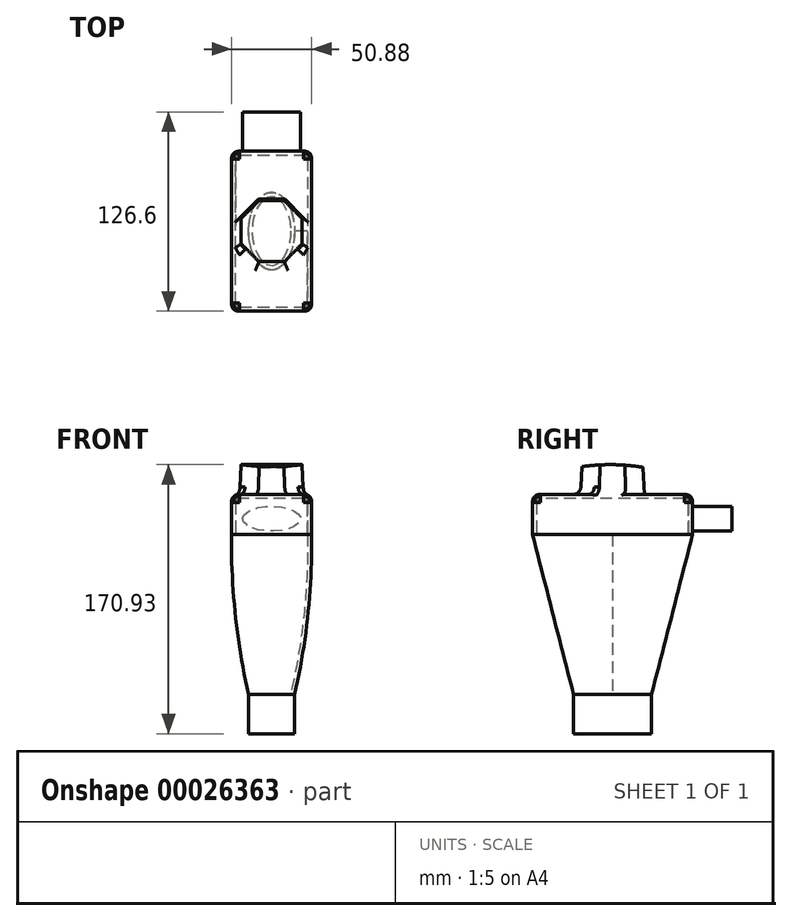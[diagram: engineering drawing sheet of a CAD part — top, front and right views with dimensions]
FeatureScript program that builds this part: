
annotation { "Feature Type Name" : "Feature", "Feature Type Description" : "" }
export const myFeature = defineFeature(function(context is Context, id is Id, definition is map)
    precondition{}
    {
        {
            var Q0;
            Q0=qCreatedBy(makeId("Top.planeOp"),FACE);
            var sketch = newSketch(context, id + "F0", { "sketchPlane" : qUnion([Q0])});
            skLineSegment(sketch, "E0.rect.bottom", {"start": v(-25.4, 50.8) * mm, "end": v(25.4, 50.8) * mm});
            skLineSegment(sketch, "E0.rect.top", {"start": v(-25.4, -50.8) * mm, "end": v(25.4, -50.8) * mm});
            skLineSegment(sketch, "E0.rect.left", {"start": v(-25.4, 50.8) * mm, "end": v(-25.4, -50.8) * mm});
            skLineSegment(sketch, "E0.rect.right", {"start": v(25.4, 50.8) * mm, "end": v(25.4, -50.8) * mm});
            skPoint(sketch, "E0.rect.middle", {"position": v(0, 0) * mm});
            skSolve(sketch);
        }
        {
            var Q0;
            Q0 = qSketchRegion(id + "F0", true);
            extrude(context, id + "F1", {"entities" : qUnion([Q0]), "depth" : 25.4 * mm});
        }
        {
            var Q0;
            Q0=makeQuery(id+"F1.opExtrude","CAP_EDGE",EDGE,{"disambiguationData":[OSD([sQuery(id+"F0.wireOp",EDGE,"E0.rect.top")])],"isStart":false});
            var Q1;
            Q1=makeQuery(id+"F1.opExtrude","CAP_EDGE",EDGE,{"disambiguationData":[OSD([sQuery(id+"F0.wireOp",EDGE,"E0.rect.right")])],"isStart":false});
            var Q2;
            Q2=makeQuery(id+"F1.opExtrude","CAP_EDGE",EDGE,{"disambiguationData":[OSD([sQuery(id+"F0.wireOp",EDGE,"E0.rect.bottom")])],"isStart":false});
            var Q3;
            Q3=makeQuery(id+"F1.opExtrude","CAP_EDGE",EDGE,{"disambiguationData":[OSD([sQuery(id+"F0.wireOp",EDGE,"E0.rect.left")])],"isStart":false});
            var Q4;
            Q4=makeQuery(id+"F1.opExtrude","SWEPT_EDGE",EDGE,{"disambiguationData":[OSD([sQuery(id+"F0.wireOp",EDGE,"E0.rect.top"),sQuery(id+"F0.wireOp",EDGE,"E0.rect.right")])]});
            var Q5;
            Q5=makeQuery(id+"F1.opExtrude","SWEPT_EDGE",EDGE,{"disambiguationData":[OSD([sQuery(id+"F0.wireOp",EDGE,"E0.rect.top"),sQuery(id+"F0.wireOp",EDGE,"E0.rect.left")])]});
            var Q6;
            Q6=makeQuery(id+"F1.opExtrude","SWEPT_EDGE",EDGE,{"disambiguationData":[OSD([sQuery(id+"F0.wireOp",EDGE,"E0.rect.bottom"),sQuery(id+"F0.wireOp",EDGE,"E0.rect.right")])]});
            var Q7;
            Q7=makeQuery(id+"F1.opExtrude","SWEPT_EDGE",EDGE,{"disambiguationData":[OSD([sQuery(id+"F0.wireOp",EDGE,"E0.rect.bottom"),sQuery(id+"F0.wireOp",EDGE,"E0.rect.left")])]});
            fillet(context, id + "F2", {"entities" : qUnion([Q0, Q1, Q2, Q3, Q4, Q5, Q6, Q7]), "radius" : 5.08 * mm, "tangentPropagation" : true, "rho" : 0.5, "crossSection" : FilletCrossSection.CONIC, "allowEdgeOverflow" : false});
        }
        {
            var Q0;
            Q0=makeQuery(id+"F1.opExtrude","CAP_FACE",FACE,{"disambiguationData":[OSD([sQuery(id+"F0.wireOp",EDGE,"E0.rect.bottom"),sQuery(id+"F0.wireOp",EDGE,"E0.rect.top"),sQuery(id+"F0.wireOp",EDGE,"E0.rect.left"),sQuery(id+"F0.wireOp",EDGE,"E0.rect.right")])],"isStart":true});
            cPlane(context, id + "F3", {"entities" : qUnion([Q0]), "cplaneType" : CPlaneType.OFFSET, "offset" : 101.6 * mm, "width" : 152.4 * mm, "height" : 152.4 * mm});
        }
        {
            var Q0;
            Q0=qCreatedBy(id+"F3.planeOp",FACE);
            var sketch = newSketch(context, id + "F4", { "sketchPlane" : qUnion([Q0])});
            skEllipse(sketch, "E1", {"center": v(0, 0) * mm, "majorRadius": 24.72 * mm, "minorRadius": 14.6 * mm, "majorAxis": v(0, 1)});
            skSolve(sketch);
        }
        {
            var Q0;
            Q0=qCreatedBy(makeId("Front.planeOp"),FACE);
            var sketch = newSketch(context, id + "F5", { "sketchPlane" : qUnion([Q0])});
            skArc(sketch, "E2", {"start": v(14.6, -101.6) * mm, "mid": v(23.05, -51.12) * mm, "end": v(25.4, 0) * mm});
            skLineSegment(sketch, "E3", {"start": v(0, 0) * mm, "end": v(0, -101.81) * mm, "construction": true});
            skArc(sketch, "E4.MirrorCS", {"start": v(-14.6, -101.6) * mm, "mid": v(-23.05, -51.12) * mm, "end": v(-25.4, 0) * mm});
            skSolve(sketch);
        }
        {
            var Q1;
            Q1=makeQuery(id+"F1.opExtrude","CAP_FACE",FACE,{"disambiguationData":[OSD([sQuery(id+"F0.wireOp",EDGE,"E0.rect.bottom"),sQuery(id+"F0.wireOp",EDGE,"E0.rect.top"),sQuery(id+"F0.wireOp",EDGE,"E0.rect.left"),sQuery(id+"F0.wireOp",EDGE,"E0.rect.right")])],"isStart":true});
            var Q2;
            Q2=makeQuery(id+"F4.imprint","IMPRINT",FACE,{"disambiguationData":[TD([[makeQuery(id+"F4.imprint","IMPRINT",EDGE,{"derivedFrom":sQuery(id+"F4.wireOp",EDGE,"E1")}),1.0]])]});
            var Q3;
            Q3=sQuery(id+"F5.wireOp",EDGE,"E2");
            var Q4;
            Q4=sQuery(id+"F5.wireOp",EDGE,"E4.MirrorCS");
            loft(context, id + "F6", {"operationType" : NewBodyOperationType.ADD, "addGuides" : true, "sheetProfilesArray" : [{ "sheetProfileEntities" : qUnion([Q1]) }, { "sheetProfileEntities" : qUnion([Q2]) }], "guidesArray" : [{ "guideEntities" : qUnion([Q3]), "guideDerivativeType" : LoftGuideDerivativeType.DEFAULT, "guideDerivativeMagnitude" : 1 }, { "guideEntities" : qUnion([Q4]), "guideDerivativeType" : LoftGuideDerivativeType.DEFAULT, "guideDerivativeMagnitude" : 1 }]});
        }
        {
            var Q0;
            Q0=makeQuery(id+"F6.opLoft","CAP_FACE",FACE,{"disambiguationData":[OSD([makeQuery(id+"F4.imprint","IMPRINT",FACE,{"disambiguationData":[TD([[makeQuery(id+"F4.imprint","IMPRINT",EDGE,{"derivedFrom":sQuery(id+"F4.wireOp",EDGE,"E1")}),1.0]])]})])],"isStart":true});
            shell(context, id + "F7", {"entities" : qUnion([Q0]), "thickness" : 2.5 * mm});
        }
        {
            var Q0;
            Q0=qCreatedBy(makeId("Right.planeOp"),FACE);
            var sketch = newSketch(context, id + "F8", { "sketchPlane" : qUnion([Q0])});
            skArc(sketch, "E5", {"start": v(71.34, 21.87) * mm, "mid": v(-1.54, 44.33) * mm, "end": v(-74.42, 21.87) * mm});
            skSolve(sketch);
        }
        {
            var Q0;
            Q0=sQuery(id+"F8.wireOp",EDGE,"E5");
            extrude(context, id + "F9", {"bodyType" : ToolBodyType.SURFACE, "surfaceEntities" : qUnion([Q0]), "depth" : 25 * mm, "hasSecondDirection" : true, "secondDirectionOppositeDirection" : true, "secondDirectionDepth" : 25 * mm});
        }
        {
            var Q0;
            Q0=makeQuery(id+"F4.imprint","IMPRINT",FACE,{"disambiguationData":[TD([[makeQuery(id+"F4.imprint","IMPRINT",EDGE,{"derivedFrom":sQuery(id+"F4.wireOp",EDGE,"E1")}),1.0]])]});
            var sketch = newSketch(context, id + "F10", { "sketchPlane" : qUnion([Q0])});
            skEllipse(sketch, "E6.0", {"center": v(0, 0) * mm, "majorRadius": 24.72 * mm, "minorRadius": 14.6 * mm, "majorAxis": v(0, 1)});
            skFitSpline(sketch, "E7.0", {"points": [v(6.07, 18.9) * mm, v(5.05, 19.91) * mm, v(4.15, 20.63) * mm, v(3.44, 21.1) * mm, v(2.68, 21.51) * mm, v(1.88, 21.84) * mm, v(1.05, 22.06) * mm, v(0.18, 22.16) * mm, v(-0.68, 22.12) * mm, v(-1.38, 21.97) * mm, v(-1.94, 21.8) * mm, v(-2.47, 21.6) * mm, v(-3.1, 21.3) * mm, v(-3.83, 20.85) * mm, v(-4.52, 20.34) * mm, v(-5.17, 19.78) * mm, v(-5.98, 18.99) * mm, v(-6.9, 17.9) * mm, v(-7.86, 16.49) * mm, v(-8.7, 15) * mm, v(-9.44, 13.45) * mm, v(-10.28, 11.33) * mm, v(-11.09, 8.62) * mm, v(-11.62, 5.8) * mm, v(-11.88, 3.54) * mm, v(-12, 1.84) * mm, v(-12.04, 0.14) * mm, v(-12.02, -1.56) * mm, v(-11.9, -3.27) * mm, v(-11.72, -4.96) * mm, v(-11.46, -6.63) * mm, v(-11.12, -8.29) * mm, v(-10.7, -9.92) * mm, v(-10.19, -11.53) * mm, v(-9.58, -13.12) * mm, v(-8.86, -14.68) * mm, v(-8.05, -16.18) * mm, v(-7.1, -17.61) * mm, v(-6.2, -18.73) * mm, v(-5.41, -19.56) * mm, v(-4.77, -20.14) * mm, v(-4.1, -20.66) * mm, v(-3.38, -21.13) * mm, v(-2.62, -21.54) * mm, v(-1.82, -21.86) * mm, v(-1, -22.07) * mm, v(-0.12, -22.16) * mm, v(0.74, -22.1) * mm, v(1.44, -21.96) * mm, v(1.99, -21.78) * mm, v(2.52, -21.58) * mm, v(3.15, -21.26) * mm, v(3.87, -20.82) * mm, v(4.56, -20.31) * mm, v(5.2, -19.75) * mm, v(6.01, -18.95) * mm, v(6.92, -17.87) * mm, v(7.88, -16.45) * mm, v(8.72, -14.97) * mm, v(9.45, -13.42) * mm, v(10.29, -11.3) * mm, v(11.1, -8.6) * mm, v(11.62, -5.79) * mm, v(11.88, -3.53) * mm, v(12, -1.84) * mm, v(12.04, -0.15) * mm, v(12.02, 1.54) * mm, v(11.9, 3.22) * mm, v(11.73, 4.9) * mm, v(11.47, 6.58) * mm, v(11.01, 8.82) * mm, v(10.4, 10.99) * mm, v(9.6, 13.09) * mm, v(8.9, 14.62) * mm, v(8.09, 16.12) * mm, v(7.15, 17.56) * mm, v(6.07, 18.9) * mm, v(5.05, 19.91) * mm, v(4.15, 20.63) * mm, v(6.07, 18.9) * mm]});
            skSolve(sketch);
        }
        {
            var Q0;
            Q0 = qSketchRegion(id + "F10", true);
            extrude(context, id + "F11", {"entities" : qUnion([Q0]), "operationType" : NewBodyOperationType.ADD, "depth" : 25 * mm});
        }
        {
            var Q0;
            Q0=makeQuery(id+"F1.opExtrude","CAP_FACE",FACE,{"disambiguationData":[OSD([sQuery(id+"F0.wireOp",EDGE,"E0.rect.bottom"),sQuery(id+"F0.wireOp",EDGE,"E0.rect.top"),sQuery(id+"F0.wireOp",EDGE,"E0.rect.left"),sQuery(id+"F0.wireOp",EDGE,"E0.rect.right")])],"isStart":false});
            var sketch = newSketch(context, id + "F12", { "sketchPlane" : qUnion([Q0])});
            skCircle(sketch, "E8.cCircle", {"center": v(0, 0) * mm, "radius": 20.32 * mm, "construction": true});
            skLineSegment(sketch, "E8.0", {"start": v(20.32, 8.42) * mm, "end": v(20.32, -8.42) * mm});
            skLineSegment(sketch, "E8.1", {"start": v(20.32, -8.42) * mm, "end": v(8.42, -20.32) * mm});
            skLineSegment(sketch, "E8.2", {"start": v(8.42, -20.32) * mm, "end": v(-8.42, -20.32) * mm});
            skLineSegment(sketch, "E8.3", {"start": v(-8.42, -20.32) * mm, "end": v(-20.32, -8.42) * mm});
            skLineSegment(sketch, "E8.4", {"start": v(-20.32, -8.42) * mm, "end": v(-20.32, 8.42) * mm});
            skLineSegment(sketch, "E8.5", {"start": v(-20.32, 8.42) * mm, "end": v(-8.42, 20.32) * mm});
            skLineSegment(sketch, "E8.6", {"start": v(-8.42, 20.32) * mm, "end": v(8.42, 20.32) * mm});
            skLineSegment(sketch, "E8.7", {"start": v(8.42, 20.32) * mm, "end": v(20.32, 8.42) * mm});
            skPoint(sketch, "E8.0.midPoint", {"position": v(20.32, 0) * mm});
            skSolve(sketch);
        }
        {
            var Q0;
            Q0 = qSketchRegion(id + "F12", true);
            var Q1;
            Q1=makeQuery(id+"F9.opExtrude","SWEPT_FACE",FACE,{"disambiguationData":[OSD([sQuery(id+"F8.wireOp",EDGE,"E5")])]});
            extrude(context, id + "F13", {"entities" : qUnion([Q0]), "operationType" : NewBodyOperationType.ADD, "endBound" : BoundingType.UP_TO_SURFACE, "endBoundEntityFace" : qUnion([Q1]), "depth" : 25 * mm, "hasDraft" : true, "draftAngle" : 3 * degree, "draftPullDirection" : true});
        }
        {
            var Q0;
            Q0=makeQuery(id+"F13.opExtrude","CAP_EDGE",EDGE,{"disambiguationData":[OSD([sQuery(id+"F12.wireOp",EDGE,"E8.6")])],"isStart":true});
            var Q1;
            Q1=makeQuery(id+"F13.opExtrude","CAP_EDGE",EDGE,{"disambiguationData":[OSD([sQuery(id+"F12.wireOp",EDGE,"E8.5")])],"isStart":true});
            var Q2;
            {var subQ0=sQuery(id+"F0.wireOp",EDGE,"E0.rect.left");Q2=makeQuery(id+"F13.boolean.opBoolean","MERGE",EDGE,{"derivedFrom":[makeQuery(id+"F2.opFillet","BLEND_EDGE",EDGE,{"blendedFrom":[makeQuery(id+"F1.opExtrude","CAP_EDGE",EDGE,{"disambiguationData":[OSD([subQ0])],"isStart":false}),makeQuery(id+"F1.opExtrude","CAP_FACE",FACE,{"disambiguationData":[OSD([sQuery(id+"F0.wireOp",EDGE,"E0.rect.bottom"),sQuery(id+"F0.wireOp",EDGE,"E0.rect.top"),subQ0,sQuery(id+"F0.wireOp",EDGE,"E0.rect.right")])],"isStart":false})],"blendedInto":[makeQuery(id+"F1.opExtrude","CAP_FACE",FACE,{"disambiguationData":[OSD([sQuery(id+"F0.wireOp",EDGE,"E0.rect.bottom"),sQuery(id+"F0.wireOp",EDGE,"E0.rect.top"),subQ0,sQuery(id+"F0.wireOp",EDGE,"E0.rect.right")])],"isStart":false})]}),makeQuery(id+"F13.opExtrude","CAP_EDGE",EDGE,{"disambiguationData":[OSD([sQuery(id+"F12.wireOp",EDGE,"E8.4")])],"isStart":true})]});}
            var Q3;
            Q3=makeQuery(id+"F13.opExtrude","CAP_EDGE",EDGE,{"disambiguationData":[OSD([sQuery(id+"F12.wireOp",EDGE,"E8.3")])],"isStart":true});
            var Q4;
            Q4=makeQuery(id+"F13.opExtrude","CAP_EDGE",EDGE,{"disambiguationData":[OSD([sQuery(id+"F12.wireOp",EDGE,"E8.2")])],"isStart":true});
            var Q5;
            Q5=makeQuery(id+"F13.opExtrude","CAP_EDGE",EDGE,{"disambiguationData":[OSD([sQuery(id+"F12.wireOp",EDGE,"E8.1")])],"isStart":true});
            var Q6;
            {var subQ0=sQuery(id+"F0.wireOp",EDGE,"E0.rect.right");Q6=makeQuery(id+"F13.boolean.opBoolean","MERGE",EDGE,{"derivedFrom":[makeQuery(id+"F2.opFillet","BLEND_EDGE",EDGE,{"blendedFrom":[makeQuery(id+"F1.opExtrude","CAP_EDGE",EDGE,{"disambiguationData":[OSD([subQ0])],"isStart":false}),makeQuery(id+"F1.opExtrude","CAP_FACE",FACE,{"disambiguationData":[OSD([sQuery(id+"F0.wireOp",EDGE,"E0.rect.bottom"),sQuery(id+"F0.wireOp",EDGE,"E0.rect.top"),sQuery(id+"F0.wireOp",EDGE,"E0.rect.left"),subQ0])],"isStart":false})],"blendedInto":[makeQuery(id+"F1.opExtrude","CAP_FACE",FACE,{"disambiguationData":[OSD([sQuery(id+"F0.wireOp",EDGE,"E0.rect.bottom"),sQuery(id+"F0.wireOp",EDGE,"E0.rect.top"),sQuery(id+"F0.wireOp",EDGE,"E0.rect.left"),subQ0])],"isStart":false})]}),makeQuery(id+"F13.opExtrude","CAP_EDGE",EDGE,{"disambiguationData":[OSD([sQuery(id+"F12.wireOp",EDGE,"E8.0")])],"isStart":true})]});}
            var Q7;
            Q7=makeQuery(id+"F13.opExtrude","CAP_EDGE",EDGE,{"disambiguationData":[OSD([sQuery(id+"F12.wireOp",EDGE,"E8.7")])],"isStart":true});
            fillet(context, id + "F14", {"entities" : qUnion([Q0, Q1, Q2, Q3, Q4, Q5, Q6, Q7]), "radius" : 5 * mm, "tangentPropagation" : true, "allowEdgeOverflow" : false});
        }
        {
            var Q0;
            Q0=makeQuery(id+"F1.opExtrude","SWEPT_FACE",FACE,{"disambiguationData":[OSD([sQuery(id+"F0.wireOp",EDGE,"E0.rect.bottom")])]});
            var sketch = newSketch(context, id + "F15", { "sketchPlane" : qUnion([Q0])});
            skEllipse(sketch, "E9", {"center": v(0, 10) * mm, "majorRadius": 18.4 * mm, "minorRadius": 7.91 * mm, "majorAxis": v(1, 0)});
            skSolve(sketch);
        }
        {
            var Q0;
            Q0 = qSketchRegion(id + "F15", true);
            extrude(context, id + "F16", {"entities" : qUnion([Q0]), "operationType" : NewBodyOperationType.ADD, "depth" : 25 * mm});
        }
    });
